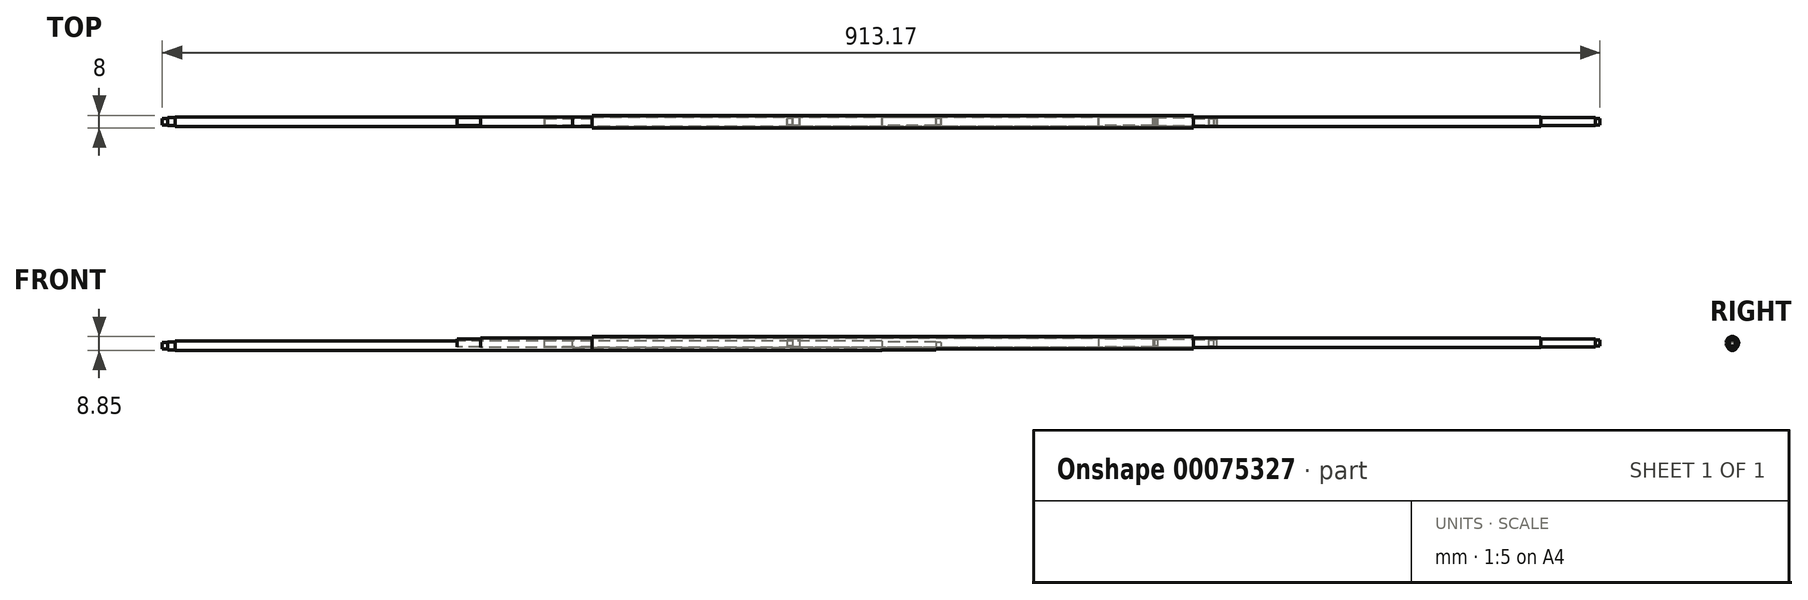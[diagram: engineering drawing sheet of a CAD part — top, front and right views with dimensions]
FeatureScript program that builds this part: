
annotation { "Feature Type Name" : "Feature", "Feature Type Description" : "" }
export const myFeature = defineFeature(function(context is Context, id is Id, definition is map)
    precondition{}
    {
        {
            var Q0;
            Q0=qCreatedBy(makeId("Front.planeOp"),FACE);
            var sketch = newSketch(context, id + "F0", { "sketchPlane" : qUnion([Q0])});
            skLineSegment(sketch, "E0", {"start": v(-55.75, 0) * mm, "end": v(-55.75, 2.5) * mm});
            skLineSegment(sketch, "E1", {"start": v(-55.75, 2.5) * mm, "end": v(-40.75, 2.5) * mm});
            skLineSegment(sketch, "E2", {"start": v(-40.75, 2.5) * mm, "end": v(-40.75, 3) * mm});
            skLineSegment(sketch, "E3", {"start": v(-40.75, 3) * mm, "end": v(351.75, 3) * mm});
            skLineSegment(sketch, "E4", {"start": v(351.75, 3) * mm, "end": v(351.75, 2.5) * mm});
            skLineSegment(sketch, "E5", {"start": v(351.75, 2.5) * mm, "end": v(386.25, 2.5) * mm});
            skLineSegment(sketch, "E6", {"start": v(386.25, 2) * mm, "end": v(389.25, 2) * mm});
            skLineSegment(sketch, "E7", {"start": v(389.25, 2) * mm, "end": v(389.25, 0) * mm});
            skLineSegment(sketch, "E8", {"start": v(-105.17, 0) * mm, "end": v(438.03, 0) * mm, "construction": true});
            skLineSegment(sketch, "E9", {"start": v(386.25, 2.5) * mm, "end": v(386.25, 2) * mm});
            skLineSegment(sketch, "E10", {"start": v(389.25, 0) * mm, "end": v(-55.75, 0) * mm});
            skSolve(sketch);
        }
        {
            var Q0;
            Q0 = qSketchRegion(id + "F0", true);
            var Q1;
            Q1=sQuery(id+"F0.wireOp",EDGE,"E8");
            revolve(context, id + "F1", {"entities" : qUnion([Q0]), "axis" : qUnion([Q1]), "revolveType" : RevolveType.FULL});
        }
        {
            var Q0;
            Q0=qCreatedBy(makeId("Front.planeOp"),FACE);
            var sketch = newSketch(context, id + "F2", { "sketchPlane" : qUnion([Q0])});
            skLineSegment(sketch, "E11", {"start": v(-22.49, 0) * mm, "end": v(33.28, 0) * mm, "construction": true});
            skLineSegment(sketch, "E12", {"start": v(153.84, 0) * mm, "end": v(153.84, 2) * mm});
            skLineSegment(sketch, "E13", {"start": v(153.84, 2) * mm, "end": v(157.34, 2) * mm});
            skLineSegment(sketch, "E14", {"start": v(667.34, 2) * mm, "end": v(670.34, 2) * mm});
            skLineSegment(sketch, "E15", {"start": v(670.34, 2) * mm, "end": v(670.34, 0) * mm});
            skLineSegment(sketch, "E16", {"start": v(153.84, 0) * mm, "end": v(670.34, 0) * mm});
            skLineSegment(sketch, "E17", {"start": v(632.84, 3) * mm, "end": v(632.84, 2.5) * mm});
            skLineSegment(sketch, "E18", {"start": v(632.84, 2.5) * mm, "end": v(667.34, 2.5) * mm});
            skLineSegment(sketch, "E19", {"start": v(667.34, 2.5) * mm, "end": v(667.34, 2) * mm});
            skLineSegment(sketch, "E20", {"start": v(157.34, 2.5) * mm, "end": v(161.84, 2.5) * mm});
            skLineSegment(sketch, "E21", {"start": v(161.84, 2.5) * mm, "end": v(161.84, 3) * mm});
            skLineSegment(sketch, "E22", {"start": v(157.34, 2.5) * mm, "end": v(157.34, 2) * mm});
            skLineSegment(sketch, "E23", {"start": v(161.84, 3) * mm, "end": v(632.84, 3) * mm});
            skSolve(sketch);
        }
        {
            var Q0;
            Q0 = qSketchRegion(id + "F2", true);
            var Q1;
            Q1=sQuery(id+"F2.wireOp",EDGE,"E16");
            revolve(context, id + "F3", {"entities" : qUnion([Q0]), "axis" : qUnion([Q1]), "revolveType" : RevolveType.FULL});
        }
        {
            var Q0;
            Q0=qCreatedBy(makeId("Front.planeOp"),FACE);
            var sketch = newSketch(context, id + "F4", { "sketchPlane" : qUnion([Q0])});
            skLineSegment(sketch, "E24", {"start": v(0, 0) * mm, "end": v(0, 2.5) * mm});
            skLineSegment(sketch, "E25", {"start": v(0, 2.5) * mm, "end": v(17.7, 2.5) * mm});
            skLineSegment(sketch, "E26", {"start": v(17.7, 2.5) * mm, "end": v(17.7, 3) * mm});
            skLineSegment(sketch, "E27", {"start": v(17.7, 3) * mm, "end": v(387.5, 3) * mm});
            skLineSegment(sketch, "E28", {"start": v(387.5, 3) * mm, "end": v(387.5, 2.5) * mm});
            skLineSegment(sketch, "E29", {"start": v(387.5, 2.5) * mm, "end": v(422, 2.5) * mm});
            skLineSegment(sketch, "E30", {"start": v(-63.17, 0) * mm, "end": v(-96, 0) * mm, "construction": true});
            skLineSegment(sketch, "E31", {"start": v(422, 2.5) * mm, "end": v(422, 2) * mm});
            skLineSegment(sketch, "E32", {"start": v(422, 2) * mm, "end": v(425, 2) * mm});
            skLineSegment(sketch, "E33", {"start": v(425, 2) * mm, "end": v(425, 0) * mm});
            skLineSegment(sketch, "E34", {"start": v(0, 0) * mm, "end": v(425, 0) * mm});
            skSolve(sketch);
        }
        {
            var Q0;
            Q0 = qSketchRegion(id + "F4", true);
            var Q1;
            Q1=sQuery(id+"F4.wireOp",EDGE,"E30");
            revolve(context, id + "F5", {"entities" : qUnion([Q0]), "axis" : qUnion([Q1]), "revolveType" : RevolveType.FULL});
        }
        {
            var Q0;
            Q0=qCreatedBy(makeId("Front.planeOp"),FACE);
            var sketch = newSketch(context, id + "F6", { "sketchPlane" : qUnion([Q0])});
            skLineSegment(sketch, "E35", {"start": v(-233.88, -1.85) * mm, "end": v(-178.1, -1.85) * mm, "construction": true});
            skLineSegment(sketch, "E36", {"start": v(-242.83, -1.85) * mm, "end": v(-242.83, 0.15) * mm});
            skLineSegment(sketch, "E37", {"start": v(-242.83, 0.15) * mm, "end": v(-239.33, 0.15) * mm});
            skLineSegment(sketch, "E38", {"start": v(-239.33, 0.15) * mm, "end": v(-239.33, 0.65) * mm});
            skLineSegment(sketch, "E39", {"start": v(-239.33, 0.65) * mm, "end": v(-234.83, 0.65) * mm});
            skLineSegment(sketch, "E40", {"start": v(-234.83, 0.65) * mm, "end": v(-234.83, 1.15) * mm});
            skLineSegment(sketch, "E41", {"start": v(-234.83, 1.15) * mm, "end": v(214.17, 1.15) * mm});
            skLineSegment(sketch, "E42", {"start": v(214.17, 1.15) * mm, "end": v(214.17, 0.65) * mm});
            skLineSegment(sketch, "E43", {"start": v(214.17, 0.65) * mm, "end": v(248.67, 0.65) * mm});
            skLineSegment(sketch, "E44", {"start": v(248.67, 0.65) * mm, "end": v(248.67, 0.15) * mm});
            skLineSegment(sketch, "E45", {"start": v(248.67, 0.15) * mm, "end": v(251.67, 0.15) * mm});
            skLineSegment(sketch, "E46", {"start": v(251.67, 0.15) * mm, "end": v(251.67, -1.85) * mm});
            skLineSegment(sketch, "E47", {"start": v(-242.83, -1.85) * mm, "end": v(251.67, -1.85) * mm});
            skSolve(sketch);
        }
        {
            var Q0;
            Q0 = qSketchRegion(id + "F6", true);
            var Q1;
            Q1=sQuery(id+"F6.wireOp",EDGE,"E47");
            revolve(context, id + "F7", {"entities" : qUnion([Q0]), "axis" : qUnion([Q1]), "revolveType" : RevolveType.FULL});
        }
        {
            var Q0;
            Q0=qCreatedBy(makeId("Front.planeOp"),FACE);
            var sketch = newSketch(context, id + "F8", { "sketchPlane" : qUnion([Q0])});
            skLineSegment(sketch, "E48", {"start": v(0, 0) * mm, "end": v(0, 2.15) * mm});
            skLineSegment(sketch, "E49", {"start": v(0, 2.15) * mm, "end": v(30, 2.15) * mm});
            skLineSegment(sketch, "E50", {"start": v(30, 2.15) * mm, "end": v(30, 4) * mm});
            skLineSegment(sketch, "E51", {"start": v(30, 4) * mm, "end": v(412, 4) * mm});
            skLineSegment(sketch, "E52", {"start": v(412, 4) * mm, "end": v(412, 2.15) * mm});
            skLineSegment(sketch, "E53", {"start": v(412, 2.15) * mm, "end": v(427, 2.15) * mm});
            skLineSegment(sketch, "E54", {"start": v(427, 2.15) * mm, "end": v(427, 0) * mm});
            skLineSegment(sketch, "E55", {"start": v(427, 0) * mm, "end": v(0, 0) * mm});
            skSolve(sketch);
        }
        {
            var Q0;
            Q0 = qSketchRegion(id + "F8", true);
            var Q1;
            Q1=sQuery(id+"F8.wireOp",EDGE,"E55");
            revolve(context, id + "F9", {"entities" : qUnion([Q0]), "axis" : qUnion([Q1]), "revolveType" : RevolveType.FULL});
        }
    });
